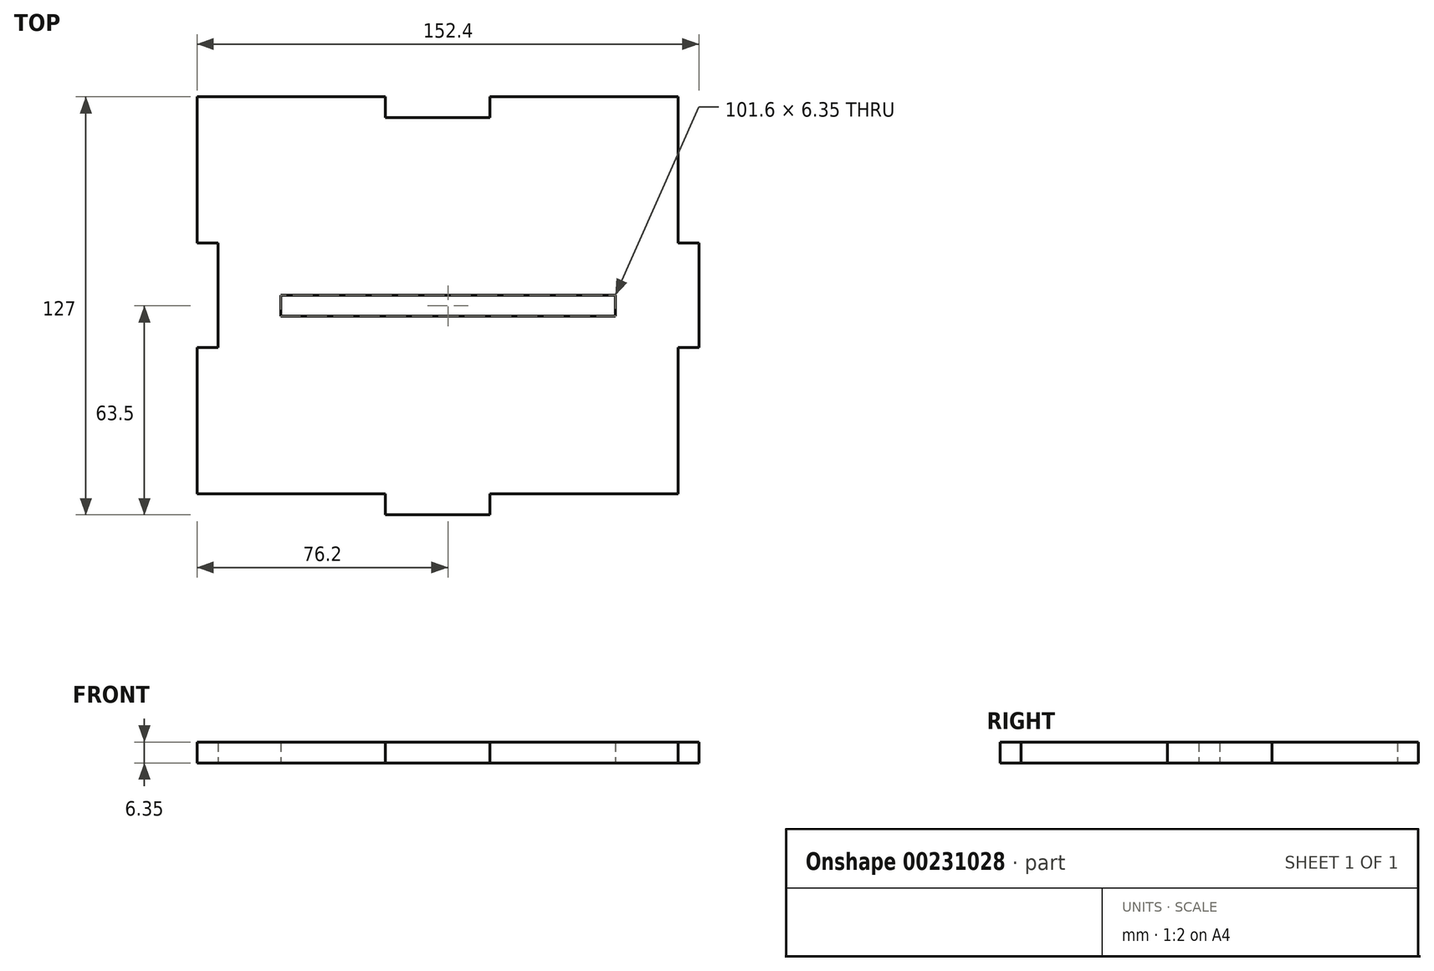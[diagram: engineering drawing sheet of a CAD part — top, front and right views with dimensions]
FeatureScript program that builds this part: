
annotation { "Feature Type Name" : "Feature", "Feature Type Description" : "" }
export const myFeature = defineFeature(function(context is Context, id is Id, definition is map)
    precondition{}
    {
        {
            var Q0;
            Q0=qCreatedBy(makeId("Top.planeOp"),FACE);
            var sketch = newSketch(context, id + "F0", { "sketchPlane" : qUnion([Q0])});
            skLineSegment(sketch, "E0.right", {"start": v(-76.2, 63.5) * mm, "end": v(-76.2, 57.15) * mm});
            skPoint(sketch, "E0.middle", {"position": v(0, 0) * mm});
            skLineSegment(sketch, "E1.MirrorCS", {"start": v(12.7, 63.5) * mm, "end": v(12.7, 57.15) * mm});
            skLineSegment(sketch, "E2.MirrorCS", {"start": v(-76.2, 19.05) * mm, "end": v(-69.85, 19.05) * mm});
            skLineSegment(sketch, "E3.MirrorCS", {"start": v(-76.2, -12.7) * mm, "end": v(-69.85, -12.7) * mm});
            skLineSegment(sketch, "E4.MirrorCS", {"start": v(-76.2, -57.15) * mm, "end": v(-69.85, -57.15) * mm});
            skLineSegment(sketch, "E5.MirrorCS", {"start": v(-76.2, -57.15) * mm, "end": v(-63.5, -57.15) * mm});
            skLineSegment(sketch, "E6.MirrorCS", {"start": v(76.2, 19.05) * mm, "end": v(69.85, 19.05) * mm});
            skLineSegment(sketch, "E7.MirrorCS", {"start": v(76.2, -12.7) * mm, "end": v(69.85, -12.7) * mm});
            skLineSegment(sketch, "E8.trimOffspring", {"start": v(-6.35, -63.5) * mm, "end": v(-12.7, -63.5) * mm});
            skLineSegment(sketch, "E9.trimOffspring", {"start": v(6.35, -63.5) * mm, "end": v(0, -63.5) * mm});
            skLineSegment(sketch, "E10.trimOffspring", {"start": v(76.2, -6.35) * mm, "end": v(76.2, -12.7) * mm});
            skLineSegment(sketch, "E11.trimOffspring", {"start": v(76.2, 6.35) * mm, "end": v(76.2, 0) * mm});
            skLineSegment(sketch, "E12.trimOffspring", {"start": v(76.2, 19.05) * mm, "end": v(76.2, 12.7) * mm});
            skLineSegment(sketch, "E13.trimOffspring", {"start": v(63.5, 63.5) * mm, "end": v(57.15, 63.5) * mm});
            skLineSegment(sketch, "E14.trimOffspring", {"start": v(50.8, 63.5) * mm, "end": v(44.45, 63.5) * mm});
            skLineSegment(sketch, "E15.trimOffspring", {"start": v(38.1, 63.5) * mm, "end": v(31.75, 63.5) * mm});
            skLineSegment(sketch, "E16.trimOffspring", {"start": v(25.4, 63.5) * mm, "end": v(19.05, 63.5) * mm});
            skLineSegment(sketch, "E17.trimOffspring", {"start": v(-25.4, 63.5) * mm, "end": v(-31.75, 63.5) * mm});
            skLineSegment(sketch, "E18.trimOffspring", {"start": v(-38.1, 63.5) * mm, "end": v(-44.45, 63.5) * mm});
            skLineSegment(sketch, "E19.trimOffspring", {"start": v(-50.8, 63.5) * mm, "end": v(-57.15, 63.5) * mm});
            skLineSegment(sketch, "E20.trimOffspring", {"start": v(-63.5, 63.5) * mm, "end": v(-76.2, 63.5) * mm});
            skLineSegment(sketch, "E21.trimOffspring", {"start": v(-76.2, 50.8) * mm, "end": v(-76.2, 44.45) * mm});
            skLineSegment(sketch, "E22.trimOffspring", {"start": v(-76.2, 38.1) * mm, "end": v(-76.2, 31.75) * mm});
            skLineSegment(sketch, "E23.trimOffspring", {"start": v(-76.2, 25.4) * mm, "end": v(-76.2, 19.05) * mm});
            skLineSegment(sketch, "E24.trimOffspring", {"start": v(-76.2, -12.7) * mm, "end": v(-76.2, -19.05) * mm});
            skLineSegment(sketch, "E25.trimOffspring", {"start": v(-76.2, -25.4) * mm, "end": v(-76.2, -31.75) * mm});
            skLineSegment(sketch, "E26.trimOffspring", {"start": v(-76.2, -38.1) * mm, "end": v(-76.2, -44.45) * mm});
            skLineSegment(sketch, "E27.trimOffspring", {"start": v(-76.2, -50.8) * mm, "end": v(-76.2, -57.15) * mm});
            skLineSegment(sketch, "E28.bottom", {"start": v(50.8, 3.17) * mm, "end": v(-50.8, 3.18) * mm});
            skLineSegment(sketch, "E28.top", {"start": v(50.8, -3.18) * mm, "end": v(-50.8, -3.17) * mm});
            skLineSegment(sketch, "E28.left", {"start": v(50.8, 3.17) * mm, "end": v(50.8, -3.18) * mm});
            skLineSegment(sketch, "E28.right", {"start": v(-50.8, 3.18) * mm, "end": v(-50.8, -3.17) * mm});
            skPoint(sketch, "E29.orphan", {"position": v(-69.85, 63.5) * mm});
            skLineSegment(sketch, "E30.trimOffspring", {"start": v(-12.7, 57.15) * mm, "end": v(-6.35, 57.15) * mm});
            skLineSegment(sketch, "E31.trimOffspring", {"start": v(0, 57.15) * mm, "end": v(6.35, 57.15) * mm});
            skLineSegment(sketch, "E32.trimOffspring", {"start": v(69.85, 50.8) * mm, "end": v(69.85, 44.45) * mm});
            skLineSegment(sketch, "E33.trimOffspring", {"start": v(69.85, 38.1) * mm, "end": v(69.85, 31.75) * mm});
            skLineSegment(sketch, "E34.trimOffspring", {"start": v(69.85, 25.4) * mm, "end": v(69.85, 19.05) * mm});
            skLineSegment(sketch, "E35.trimOffspring", {"start": v(-69.85, 19.05) * mm, "end": v(-69.85, 12.7) * mm});
            skLineSegment(sketch, "E36.trimOffspring", {"start": v(-69.85, 6.35) * mm, "end": v(-69.85, 0) * mm});
            skLineSegment(sketch, "E37.trimOffspring", {"start": v(-69.85, -6.35) * mm, "end": v(-69.85, -12.7) * mm});
            skLineSegment(sketch, "E38.trimOffspring", {"start": v(-57.15, -57.15) * mm, "end": v(-50.8, -57.15) * mm});
            skLineSegment(sketch, "E39.trimOffspring", {"start": v(-44.45, -57.15) * mm, "end": v(-38.1, -57.15) * mm});
            skLineSegment(sketch, "E40.trimOffspring", {"start": v(-31.75, -57.15) * mm, "end": v(-25.4, -57.15) * mm});
            skLineSegment(sketch, "E41.trimOffspring", {"start": v(19.05, -57.15) * mm, "end": v(25.4, -57.15) * mm});
            skLineSegment(sketch, "E42.trimOffspring", {"start": v(31.75, -57.15) * mm, "end": v(38.1, -57.15) * mm});
            skLineSegment(sketch, "E43.trimOffspring", {"start": v(44.45, -57.15) * mm, "end": v(50.8, -57.15) * mm});
            skLineSegment(sketch, "E44.trimOffspring", {"start": v(57.15, -57.15) * mm, "end": v(63.5, -57.15) * mm});
            skLineSegment(sketch, "E45.trimOffspring", {"start": v(69.85, -50.8) * mm, "end": v(69.85, -57.15) * mm});
            skLineSegment(sketch, "E46.trimOffspring", {"start": v(69.85, -38.1) * mm, "end": v(69.85, -44.45) * mm});
            skLineSegment(sketch, "E47.trimOffspring", {"start": v(69.85, -25.4) * mm, "end": v(69.85, -31.75) * mm});
            skLineSegment(sketch, "E48.trimOffspring", {"start": v(69.85, -12.7) * mm, "end": v(69.85, -19.05) * mm});
            skLineSegment(sketch, "E49", {"start": v(-12.7, -63.5) * mm, "end": v(6.35, -63.5) * mm});
            skLineSegment(sketch, "E50", {"start": v(-63.5, -57.15) * mm, "end": v(-19.05, -57.15) * mm});
            skLineSegment(sketch, "E51", {"start": v(12.7, -57.15) * mm, "end": v(57.15, -57.15) * mm});
            skLineSegment(sketch, "E52", {"start": v(63.5, -57.15) * mm, "end": v(69.85, -57.15) * mm});
            skLineSegment(sketch, "E53.MirrorCS", {"start": v(12.7, -63.5) * mm, "end": v(12.7, -57.15) * mm});
            skLineSegment(sketch, "E54.MirrorCS", {"start": v(6.35, -63.5) * mm, "end": v(12.7, -63.5) * mm});
            skLineSegment(sketch, "E55.MirrorCS", {"start": v(-19.05, -57.15) * mm, "end": v(-19.05, -63.5) * mm});
            skLineSegment(sketch, "E56.MirrorCS", {"start": v(-12.7, -63.5) * mm, "end": v(-19.05, -63.5) * mm});
            skLineSegment(sketch, "E57", {"start": v(-63.5, 63.5) * mm, "end": v(-25.4, 63.5) * mm});
            skLineSegment(sketch, "E58", {"start": v(12.7, 63.5) * mm, "end": v(69.85, 63.5) * mm});
            skLineSegment(sketch, "E59", {"start": v(-19.05, 57.15) * mm, "end": v(0, 57.15) * mm});
            skLineSegment(sketch, "E60.MirrorCS", {"start": v(-25.4, 63.5) * mm, "end": v(-19.05, 63.5) * mm});
            skLineSegment(sketch, "E61.MirrorCS", {"start": v(-19.05, 63.5) * mm, "end": v(-19.05, 57.15) * mm});
            skLineSegment(sketch, "E62", {"start": v(6.35, 57.15) * mm, "end": v(12.7, 57.15) * mm});
            skLineSegment(sketch, "E63", {"start": v(-69.85, 12.7) * mm, "end": v(-69.85, -12.7) * mm});
            skLineSegment(sketch, "E64", {"start": v(-76.2, -19.05) * mm, "end": v(-76.2, -50.8) * mm});
            skLineSegment(sketch, "E65", {"start": v(-76.2, 57.15) * mm, "end": v(-76.2, 25.4) * mm});
            skLineSegment(sketch, "E66", {"start": v(69.85, 63.5) * mm, "end": v(69.85, 19.05) * mm});
            skLineSegment(sketch, "E67", {"start": v(76.2, 12.7) * mm, "end": v(76.2, -6.35) * mm});
            skLineSegment(sketch, "E68", {"start": v(69.85, -19.05) * mm, "end": v(69.85, -50.8) * mm});
            skSolve(sketch);
        }
        {
            var Q0;
            Q0 = qSketchRegion(id + "F0", true);
            extrude(context, id + "F1", {"entities" : qUnion([Q0]), "depth" : 6.35 * mm});
        }
    });
